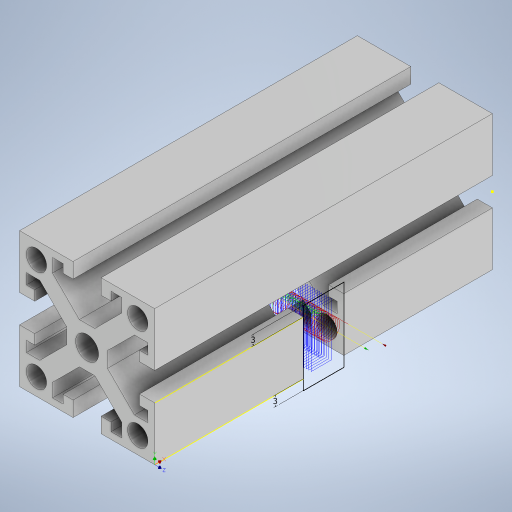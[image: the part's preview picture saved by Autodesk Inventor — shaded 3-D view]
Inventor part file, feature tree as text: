
AUTODESK INVENTOR PART (.ipt)
format: ipt  version: 2024.2 (Build 282272000, 272)  size: 422,400 bytes
history: native  units: in
note: dims shown in document units (in); Inventor stores cm internally (conversion verified against a paired STEP export)
features: sketch x3, extrude x2, plane x1
ambient origin geometry x8: Origin, YZ Plane, XZ Plane, XY Plane, X Axis, Y Axis, Z Axis, Center Point
bodies: Solid1 (feature_tree)
feature tree (6):
  extrude  "Extrusion1"  TaperAngle=45.0deg  [1 undecoded]
  plane  "Work Plane1"
  extrude  "Extrusion2"  Depth=0.2362in
  sketch  "Sketch3"  dims[d4=0.5906in d5=0.4035in d6=0.2795in d7=0.1634in d8=0.1772in d9=0.0787in d10=0.5492in d11=0.2362in d12=1.5748in d14=360.0deg d16=3.937in d17=0.0in d19=0.2362in d20=0.0in d21=0.4724in d22=0.2362in d23=0.1181in d24=0.1181in]
  sketch  "Sketch1"  dims[d0=0.2677in d1=45.0deg]
  sketch  "Sketch2"  dims[d2=0.7874in d3=0.2362in]
note: 1 required parameter value undecoded (feature->parameter linkage not recoverable at this tier; creation-order binding heuristic only, values carry confidence <= 0.55)
